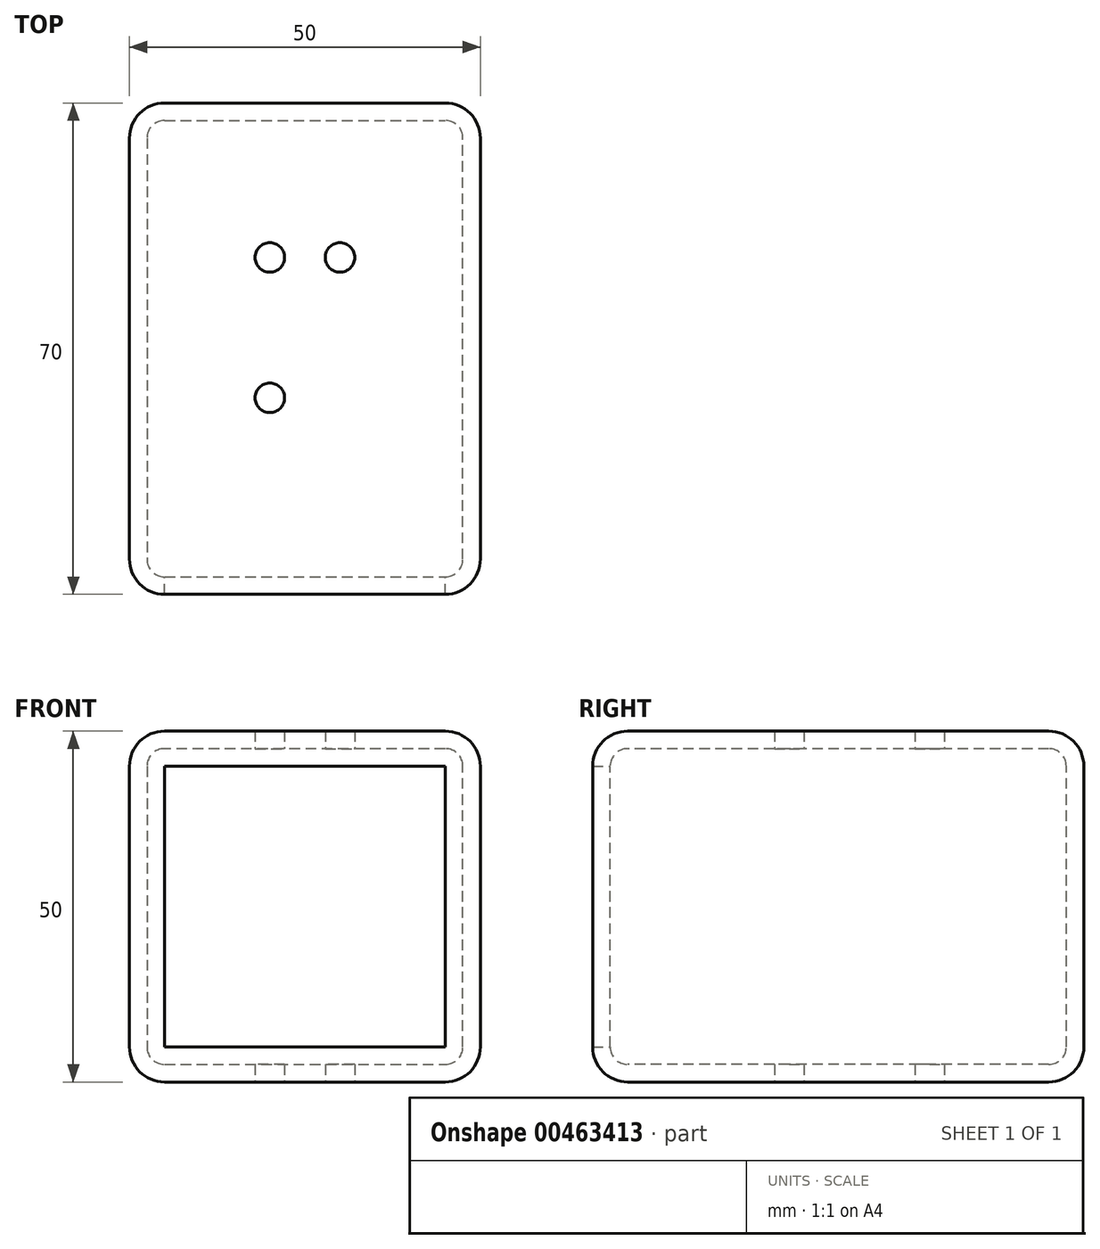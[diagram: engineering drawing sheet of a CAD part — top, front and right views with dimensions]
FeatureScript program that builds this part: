
annotation { "Feature Type Name" : "Feature", "Feature Type Description" : "" }
export const myFeature = defineFeature(function(context is Context, id is Id, definition is map)
    precondition{}
    {
        {
            var Q0;
            Q0=qCreatedBy(makeId("Front.planeOp"),FACE);
            var sketch = newSketch(context, id + "F0", { "sketchPlane" : qUnion([Q0])});
            skLineSegment(sketch, "E0", {"start": v(-20, 25) * mm, "end": v(20, 25) * mm});
            skLineSegment(sketch, "E1", {"start": v(25, 20) * mm, "end": v(25, -20) * mm});
            skLineSegment(sketch, "E2", {"start": v(20, -25) * mm, "end": v(-20, -25) * mm});
            skLineSegment(sketch, "E3", {"start": v(-25, -20) * mm, "end": v(-25, 20) * mm});
            skLineSegment(sketch, "E4", {"start": v(-25, 25) * mm, "end": v(25, -25) * mm, "construction": true});
            skPoint(sketch, "E5.visualSharp", {"position": v(-25, 25) * mm});
            skArc(sketch, "E5.filletArc", {"start": v(-20, 25) * mm, "mid": v(-23.54, 23.54) * mm, "end": v(-25, 20) * mm});
            skPoint(sketch, "E6.visualSharp", {"position": v(25, 25) * mm});
            skArc(sketch, "E6.filletArc", {"start": v(25, 20) * mm, "mid": v(23.54, 23.54) * mm, "end": v(20, 25) * mm});
            skPoint(sketch, "E7.visualSharp", {"position": v(25, -25) * mm});
            skArc(sketch, "E7.filletArc", {"start": v(20, -25) * mm, "mid": v(23.54, -23.54) * mm, "end": v(25, -20) * mm});
            skPoint(sketch, "E8.visualSharp", {"position": v(-25, -25) * mm});
            skArc(sketch, "E8.filletArc", {"start": v(-25, -20) * mm, "mid": v(-23.54, -23.54) * mm, "end": v(-20, -25) * mm});
            skSolve(sketch);
        }
        {
            var Q0;
            Q0 = qSketchRegion(id + "F0", true);
            extrude(context, id + "F1", {"entities" : qUnion([Q0]), "endBound" : BoundingType.SYMMETRIC, "oppositeDirection" : true, "depth" : 70 * mm});
        }
        {
            var Q0;
            Q0=makeQuery(id+"F1.opExtrude","CAP_FACE",FACE,{"disambiguationData":[OSD([sQuery(id+"F0.wireOp",EDGE,"E0"),sQuery(id+"F0.wireOp",EDGE,"E1"),sQuery(id+"F0.wireOp",EDGE,"E2"),sQuery(id+"F0.wireOp",EDGE,"E3"),sQuery(id+"F0.wireOp",EDGE,"E5.filletArc"),sQuery(id+"F0.wireOp",EDGE,"E6.filletArc"),sQuery(id+"F0.wireOp",EDGE,"E7.filletArc"),sQuery(id+"F0.wireOp",EDGE,"E8.filletArc")])],"isStart":false});
            var Q1;
            Q1=makeQuery(id+"F1.opExtrude","CAP_FACE",FACE,{"disambiguationData":[OSD([sQuery(id+"F0.wireOp",EDGE,"E0"),sQuery(id+"F0.wireOp",EDGE,"E1"),sQuery(id+"F0.wireOp",EDGE,"E2"),sQuery(id+"F0.wireOp",EDGE,"E3"),sQuery(id+"F0.wireOp",EDGE,"E5.filletArc"),sQuery(id+"F0.wireOp",EDGE,"E6.filletArc"),sQuery(id+"F0.wireOp",EDGE,"E7.filletArc"),sQuery(id+"F0.wireOp",EDGE,"E8.filletArc")])],"isStart":true});
            fillet(context, id + "F2", {"entities" : qUnion([Q0, Q1]), "radius" : 5 * mm, "tangentPropagation" : true, "allowEdgeOverflow" : false});
        }
        {
            var Q0;
            Q0=makeQuery(id+"F1.opExtrude","CAP_FACE",FACE,{"disambiguationData":[OSD([sQuery(id+"F0.wireOp",EDGE,"E0"),sQuery(id+"F0.wireOp",EDGE,"E1"),sQuery(id+"F0.wireOp",EDGE,"E2"),sQuery(id+"F0.wireOp",EDGE,"E3"),sQuery(id+"F0.wireOp",EDGE,"E5.filletArc"),sQuery(id+"F0.wireOp",EDGE,"E6.filletArc"),sQuery(id+"F0.wireOp",EDGE,"E7.filletArc"),sQuery(id+"F0.wireOp",EDGE,"E8.filletArc")])],"isStart":true});
            shell(context, id + "F3", {"entities" : qUnion([Q0]), "thickness" : 2.5 * mm});
        }
        {
            var Q0;
            Q0=makeQuery(id+"F1.opExtrude","SWEPT_FACE",FACE,{"disambiguationData":[OSD([sQuery(id+"F0.wireOp",EDGE,"E2")])]});
            var sketch = newSketch(context, id + "F4", { "sketchPlane" : qUnion([Q0])});
            skPoint(sketch, "E9", {"position": v(-5, -13) * mm});
            skPoint(sketch, "E10", {"position": v(5, -13) * mm});
            skPoint(sketch, "E11", {"position": v(-5, 7) * mm});
            skSolve(sketch);
        }
        {
            var Q0;
            Q0=sQuery(id+"F4.wireOp",VERTEX,"E10");
            var Q1;
            Q1=sQuery(id+"F4.wireOp",VERTEX,"E11");
            var Q2;
            Q2=sQuery(id+"F4.wireOp",VERTEX,"E9");
            var Q3;
            Q3=makeQuery(id+"F1.opExtrude","SWEPT_BODY",BODY,{"disambiguationData":[OSD([sQuery(id+"F0.wireOp",EDGE,"E0"),sQuery(id+"F0.wireOp",EDGE,"E1"),sQuery(id+"F0.wireOp",EDGE,"E2"),sQuery(id+"F0.wireOp",EDGE,"E3"),sQuery(id+"F0.wireOp",EDGE,"E5.filletArc"),sQuery(id+"F0.wireOp",EDGE,"E6.filletArc"),sQuery(id+"F0.wireOp",EDGE,"E7.filletArc"),sQuery(id+"F0.wireOp",EDGE,"E8.filletArc")])]});
            hole(context, id + "F5", {"style" : HoleStyle.SIMPLE, "endStyle" : HoleEndStyle.THROUGH, "standardTappedOrClearance" : lookupTablePath({ "standard" : "ISO", "engagement" : "75%", "pitch" : "0.8 mm", "size" : "M5", "type" : "Tapped" }), "standardBlindInLast" : lookupTablePath({ "standard" : "ISO", "engagement" : "75%", "pitch" : "0.8 mm", "size" : "M5", "type" : "Tapped" }), "holeDiameter" : 4.2 * mm, "showTappedDepth" : true, "isTappedThrough" : true, "tappedDepth" : 12 * mm, "tapClearance" : 3, "locations" : qUnion([Q0, Q1, Q2]), "scope" : qUnion([Q3]), "majorDiameter" : 5 * mm});
        }
    });
